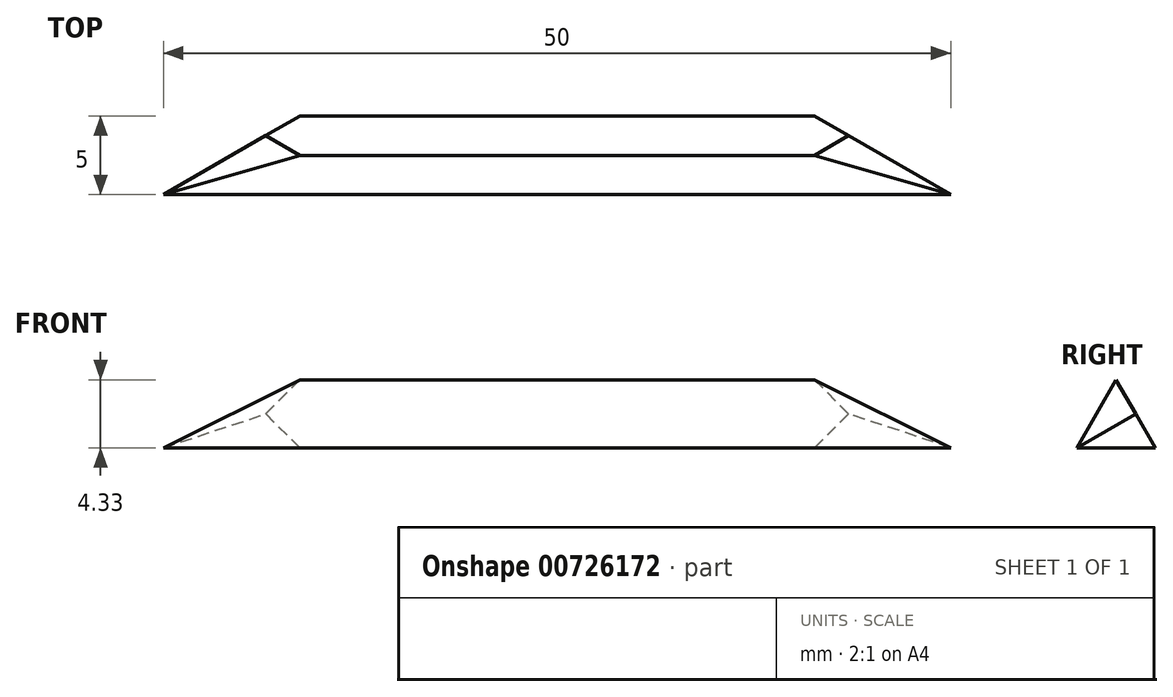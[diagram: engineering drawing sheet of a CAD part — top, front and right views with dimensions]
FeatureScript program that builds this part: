
annotation { "Feature Type Name" : "Feature", "Feature Type Description" : "" }
export const myFeature = defineFeature(function(context is Context, id is Id, definition is map)
    precondition{}
    {
        {
            var Q0;
            Q0=qCreatedBy(makeId("Right.planeOp"),FACE);
            var sketch = newSketch(context, id + "F0", { "sketchPlane" : qUnion([Q0])});
            skLineSegment(sketch, "E0", {"start": v(0, 0) * mm, "end": v(2.5, 4.33) * mm});
            skLineSegment(sketch, "E1", {"start": v(2.5, 4.33) * mm, "end": v(5, 0) * mm});
            skLineSegment(sketch, "E2", {"start": v(5, 0) * mm, "end": v(0, 0) * mm});
            skSolve(sketch);
        }
        {
            var Q0;
            Q0 = qSketchRegion(id + "F0", true);
            extrude(context, id + "F1", {"entities" : qUnion([Q0]), "depth" : 40 * mm, "offsetDistance" : 25 * mm});
        }
        {
            var Q0;
            Q0=qCreatedBy(makeId("Top.planeOp"),FACE);
            var sketch = newSketch(context, id + "F2", { "sketchPlane" : qUnion([Q0])});
            skLineSegment(sketch, "E3", {"start": v(0, 0) * mm, "end": v(17.05, 9.85) * mm});
            skLineSegment(sketch, "E4", {"start": v(17.05, 9.85) * mm, "end": v(0, 9.85) * mm});
            skLineSegment(sketch, "E5", {"start": v(0, 9.85) * mm, "end": v(0, 0) * mm});
            skSolve(sketch);
        }
        {
            var Q0;
            Q0 = qSketchRegion(id + "F2", true);
            extrude(context, id + "F3", {"entities" : qUnion([Q0]), "operationType" : NewBodyOperationType.REMOVE, "depth" : 25 * mm, "offsetDistance" : 25 * mm});
        }
        {
            var Q0;
            Q0=makeQuery(id+"F1.opExtrude","SWEPT_FACE",FACE,{"disambiguationData":[OSD([sQuery(id+"F0.wireOp",EDGE,"E0")])]});
            var sketch = newSketch(context, id + "F4", { "sketchPlane" : qUnion([Q0])});
            skLineSegment(sketch, "E6", {"start": v(0, 0) * mm, "end": v(0, 9.14) * mm});
            skLineSegment(sketch, "E7", {"start": v(0, 9.14) * mm, "end": v(15.83, 9.14) * mm});
            skLineSegment(sketch, "E8", {"start": v(15.83, 9.14) * mm, "end": v(0, 0) * mm});
            skSolve(sketch);
        }
        {
            var Q0;
            Q0 = qSketchRegion(id + "F4", true);
            extrude(context, id + "F5", {"entities" : qUnion([Q0]), "operationType" : NewBodyOperationType.REMOVE, "oppositeDirection" : true, "depth" : 25 * mm, "offsetDistance" : 25 * mm});
        }
        {
            var Q0;
            Q0=qCreatedBy(makeId("Right.planeOp"),FACE);
            cPlane(context, id + "F6", {"entities" : qUnion([Q0]), "cplaneType" : CPlaneType.OFFSET, "offset" : 25 * mm, "width" : 150 * mm, "height" : 150 * mm});
        }
        {
            var Q0;
            Q0=makeQuery(id+"F1.opExtrude","SWEPT_BODY",BODY,{"disambiguationData":[OSD([sQuery(id+"F0.wireOp",EDGE,"E0"),sQuery(id+"F0.wireOp",EDGE,"E1"),sQuery(id+"F0.wireOp",EDGE,"E2")])]});
            var Q1;
            Q1=qCreatedBy(id+"F6.planeOp",FACE);
            mirror(context, id + "F7", {"operationType" : NewBodyOperationType.ADD, "entities" : qUnion([Q0]), "mirrorPlane" : qUnion([Q1])});
        }
    });
